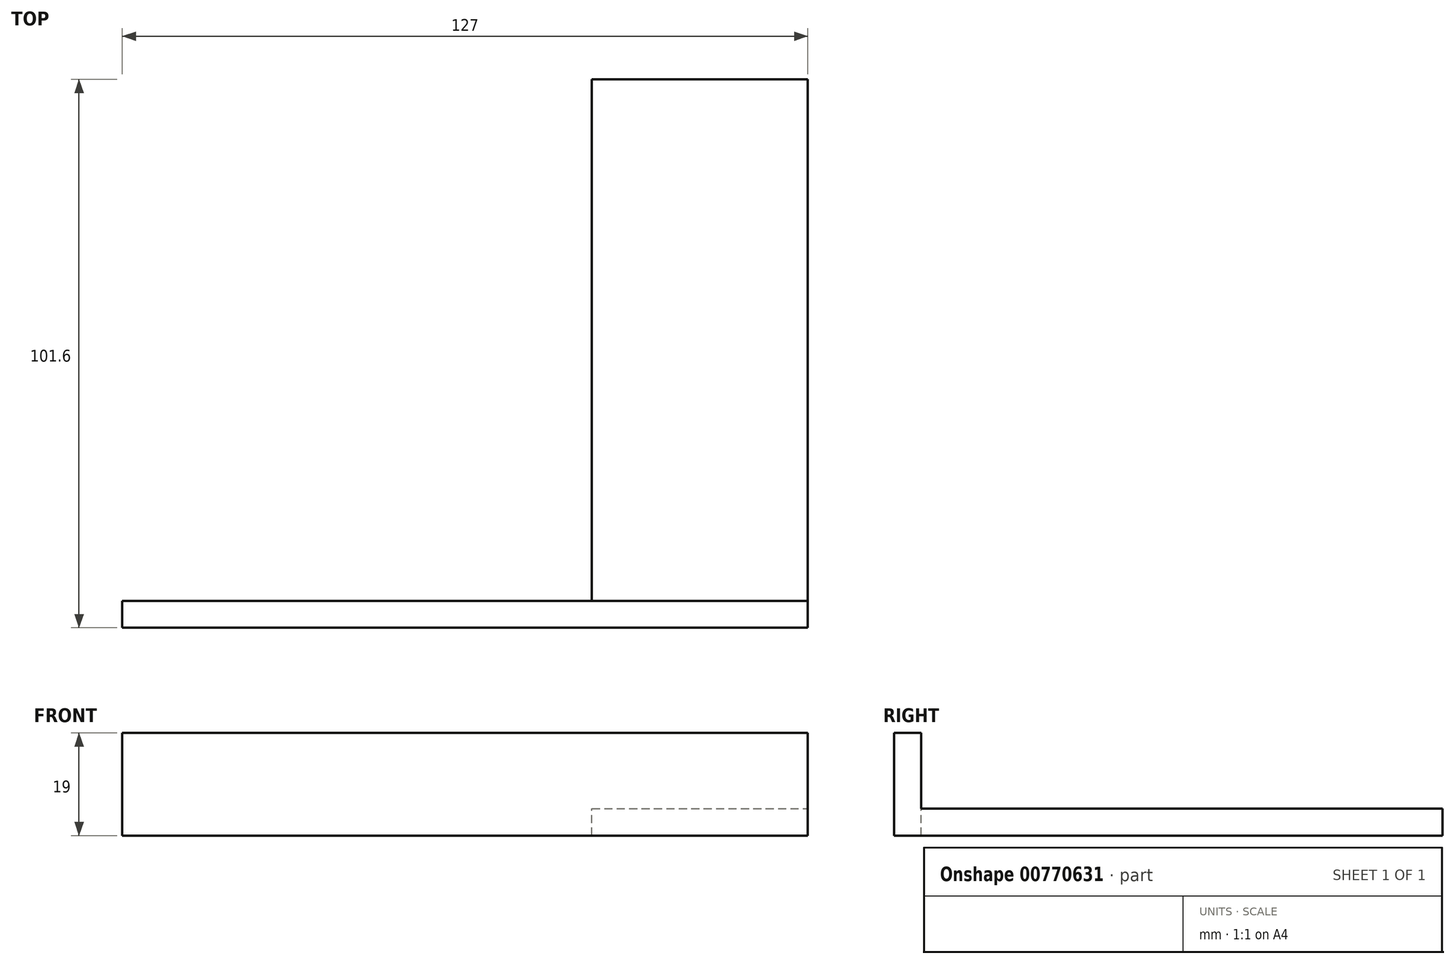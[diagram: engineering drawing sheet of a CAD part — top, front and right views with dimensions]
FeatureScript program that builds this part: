
annotation { "Feature Type Name" : "Feature", "Feature Type Description" : "" }
export const myFeature = defineFeature(function(context is Context, id is Id, definition is map)
    precondition{}
    {
        {
            var Q0;
            Q0=qCreatedBy(makeId("Top.planeOp"),FACE);
            var sketch = newSketch(context, id + "F0", { "sketchPlane" : qUnion([Q0])});
            skLineSegment(sketch, "E0", {"start": v(-20, -50.8) * mm, "end": v(-20, 50.8) * mm});
            skLineSegment(sketch, "E1", {"start": v(-20, 50.8) * mm, "end": v(20, 50.8) * mm});
            skLineSegment(sketch, "E2", {"start": v(20, 50.8) * mm, "end": v(20, -50.8) * mm});
            skLineSegment(sketch, "E3", {"start": v(20, -50.8) * mm, "end": v(-20, -50.8) * mm});
            skLineSegment(sketch, "E4", {"start": v(-20, -50.8) * mm, "end": v(-50, -50.8) * mm, "construction": true});
            skLineSegment(sketch, "E5", {"start": v(-50, -50.8) * mm, "end": v(-50, 50.8) * mm, "construction": true});
            skLineSegment(sketch, "E6", {"start": v(-50, 50.8) * mm, "end": v(-20, 50.8) * mm, "construction": true});
            skPoint(sketch, "E7", {"position": v(-50, 0) * mm});
            skPoint(sketch, "E8", {"position": v(0, -50.8) * mm});
            skSolve(sketch);
        }
        {
            var Q0;
            Q0 = qSketchRegion(id + "F0", true);
            extrude(context, id + "F1", {"entities" : qUnion([Q0]), "depth" : 5 * mm, "offsetDistance" : 25 * mm});
        }
        {
            var Q0;
            Q0=qCreatedBy(makeId("Top.planeOp"),FACE);
            var sketch = newSketch(context, id + "F2", { "sketchPlane" : qUnion([Q0])});
            skLineSegment(sketch, "E9", {"start": v(20, -45.8) * mm, "end": v(-107, -45.8) * mm});
            skLineSegment(sketch, "E10", {"start": v(-107, -50.8) * mm, "end": v(-107, -45.8) * mm});
            skLineSegment(sketch, "E11", {"start": v(20, -45.8) * mm, "end": v(20, -50.8) * mm});
            skLineSegment(sketch, "E12", {"start": v(20, -50.8) * mm, "end": v(-107, -50.8) * mm});
            skSolve(sketch);
        }
        {
            var Q0;
            Q0 = qSketchRegion(id + "F2", true);
            extrude(context, id + "F3", {"entities" : qUnion([Q0]), "operationType" : NewBodyOperationType.ADD, "depth" : 19 * mm, "offsetDistance" : 25 * mm});
        }
    });
